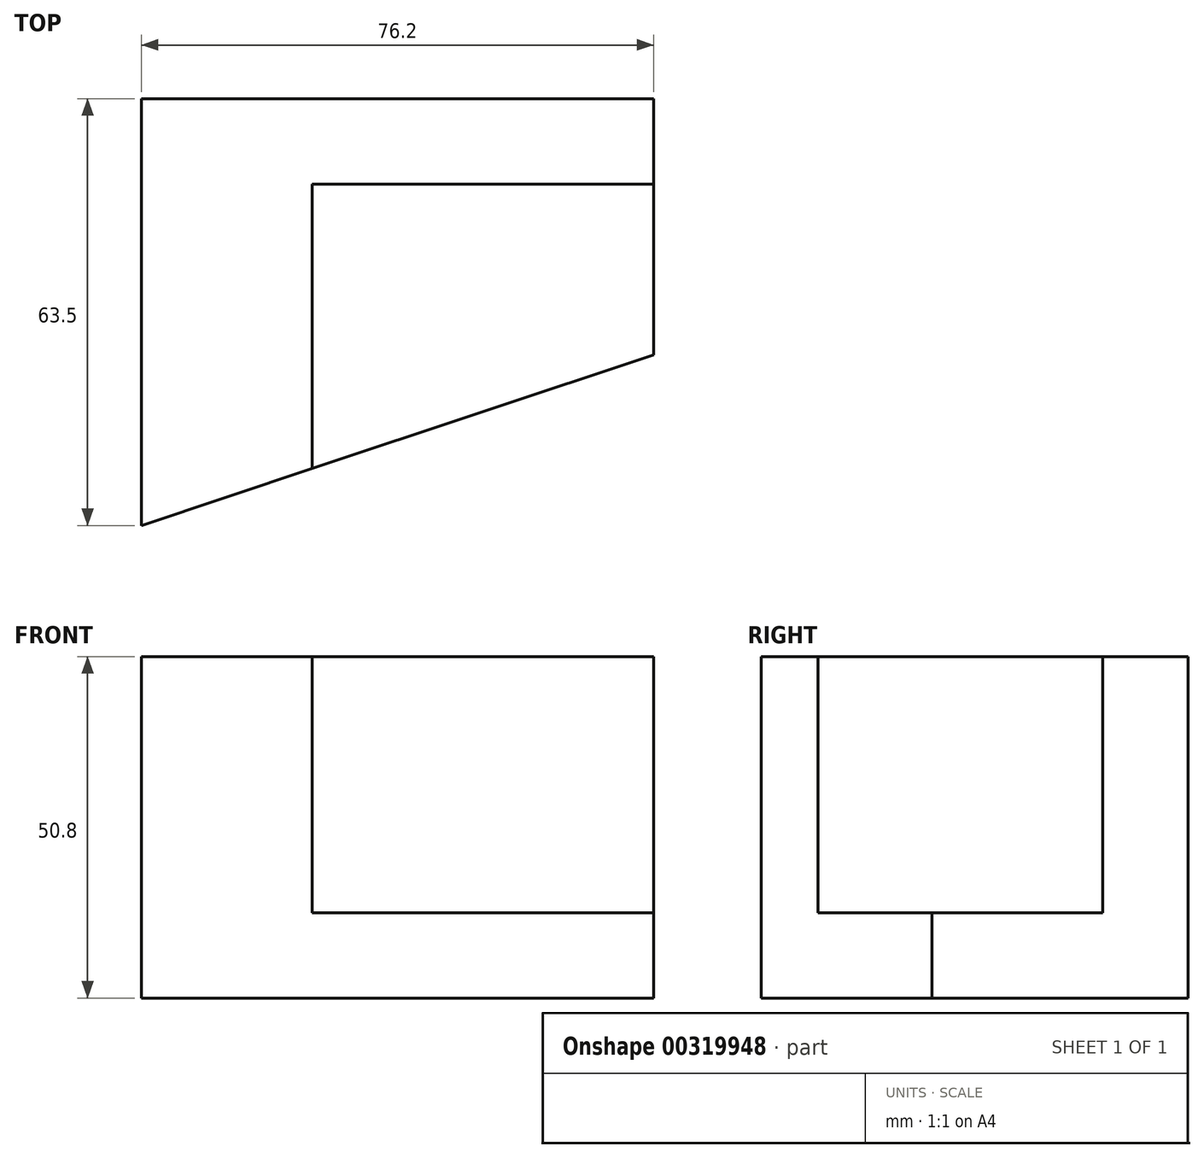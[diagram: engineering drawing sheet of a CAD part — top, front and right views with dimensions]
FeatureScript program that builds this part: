
annotation { "Feature Type Name" : "Feature", "Feature Type Description" : "" }
export const myFeature = defineFeature(function(context is Context, id is Id, definition is map)
    precondition{}
    {
        {
            var Q0;
            Q0=qCreatedBy(makeId("Front.planeOp"),FACE);
            var sketch = newSketch(context, id + "F0", { "sketchPlane" : qUnion([Q0])});
            skLineSegment(sketch, "E0", {"start": v(0, 0) * mm, "end": v(0, 50.8) * mm});
            skLineSegment(sketch, "E1", {"start": v(0, 50.8) * mm, "end": v(76.2, 50.8) * mm});
            skLineSegment(sketch, "E2", {"start": v(76.2, 50.8) * mm, "end": v(76.2, 0) * mm});
            skLineSegment(sketch, "E3", {"start": v(76.2, 0) * mm, "end": v(0, 0) * mm});
            skLineSegment(sketch, "E4", {"start": v(25.4, 50.8) * mm, "end": v(25.4, 12.7) * mm});
            skLineSegment(sketch, "E5", {"start": v(25.4, 12.7) * mm, "end": v(76.2, 12.7) * mm});
            skSolve(sketch);
        }
        {
            var Q0;
            {var subQ4=sQuery(id+"F0.wireOp",EDGE,"E0");Q0=makeQuery(id+"F0.imprint","IMPRINT",FACE,{"disambiguationData":[TD([[makeQuery(id+"F0.imprint","IMPRINT",EDGE,{"derivedFrom":subQ4}),-1.0]])]});}
            extrude(context, id + "F1", {"entities" : qUnion([Q0]), "depth" : 63.5 * mm, "symmetric" : true});
        }
        {
            var Q0;
            Q0=makeQuery(id+"F1.opExtrude","SWEPT_FACE",FACE,{"disambiguationData":[OSD([sQuery(id+"F0.wireOp",EDGE,"E1")])]});
            var sketch = newSketch(context, id + "F2", { "sketchPlane" : qUnion([Q0])});
            skLineSegment(sketch, "E6.0", {"start": v(76.2, -6.35) * mm, "end": v(76.2, 31.75) * mm});
            skLineSegment(sketch, "E7", {"start": v(0, -31.75) * mm, "end": v(76.2, -6.35) * mm});
            skLineSegment(sketch, "E8", {"start": v(0, 31.75) * mm, "end": v(0, -31.75) * mm});
            skPoint(sketch, "E9.orphan", {"position": v(76.2, -31.75) * mm});
            skLineSegment(sketch, "E10", {"start": v(76.2, 31.75) * mm, "end": v(0, 31.75) * mm});
            skLineSegment(sketch, "E11", {"start": v(0, -31.75) * mm, "end": v(76.2, -31.75) * mm});
            skLineSegment(sketch, "E12", {"start": v(76.2, -6.35) * mm, "end": v(76.2, -31.75) * mm});
            skLineSegment(sketch, "E13", {"start": v(76.2, 19.05) * mm, "end": v(25.4, 19.05) * mm});
            skSolve(sketch);
        }
        {
            var Q0;
            {var subQ0=sQuery(id+"F2.wireOp",EDGE,"E12");Q0=makeQuery(id+"F2.imprint","IMPRINT",FACE,{"disambiguationData":[TD([[makeQuery(id+"F2.imprint","IMPRINT",EDGE,{"derivedFrom":subQ0}),-1.0]])]});}
            var Q1;
            {var subQ0=sQuery(id+"F2.wireOp",EDGE,"E11");var subQ1=sQuery(id+"F2.wireOp",EDGE,"E7");var subQ2=makeQuery(id+"F2.imprint","INTERSECT",VERTEX,{"derivedFrom":[subQ1,sQuery(id+"F2.wireOp",EDGE,"E8"),subQ0]});Q1=makeQuery(id+"F2.imprint","IMPRINT",FACE,{"disambiguationData":[TD([[makeQuery(id+"F2.imprint","IMPRINT",EDGE,{"disambiguationData":[TD([[subQ2,-1.0]])],"derivedFrom":subQ1}),-1.0]])]});}
            extrude(context, id + "F3", {"entities" : qUnion([Q0, Q1]), "operationType" : NewBodyOperationType.REMOVE, "endBound" : BoundingType.THROUGH_ALL, "oppositeDirection" : true, "depth" : 25.4 * mm});
        }
        {
            var Q0;
            {var subQ3=sQuery(id+"F2.wireOp",EDGE,"E13");Q0=makeQuery(id+"F2.imprint","IMPRINT",FACE,{"disambiguationData":[TD([[makeQuery(id+"F2.imprint","IMPRINT",EDGE,{"derivedFrom":subQ3}),-1.0]])]});}
            extrude(context, id + "F4", {"entities" : qUnion([Q0]), "operationType" : NewBodyOperationType.ADD, "endBound" : BoundingType.UP_TO_NEXT, "oppositeDirection" : true, "depth" : 25.4 * mm});
        }
    });
